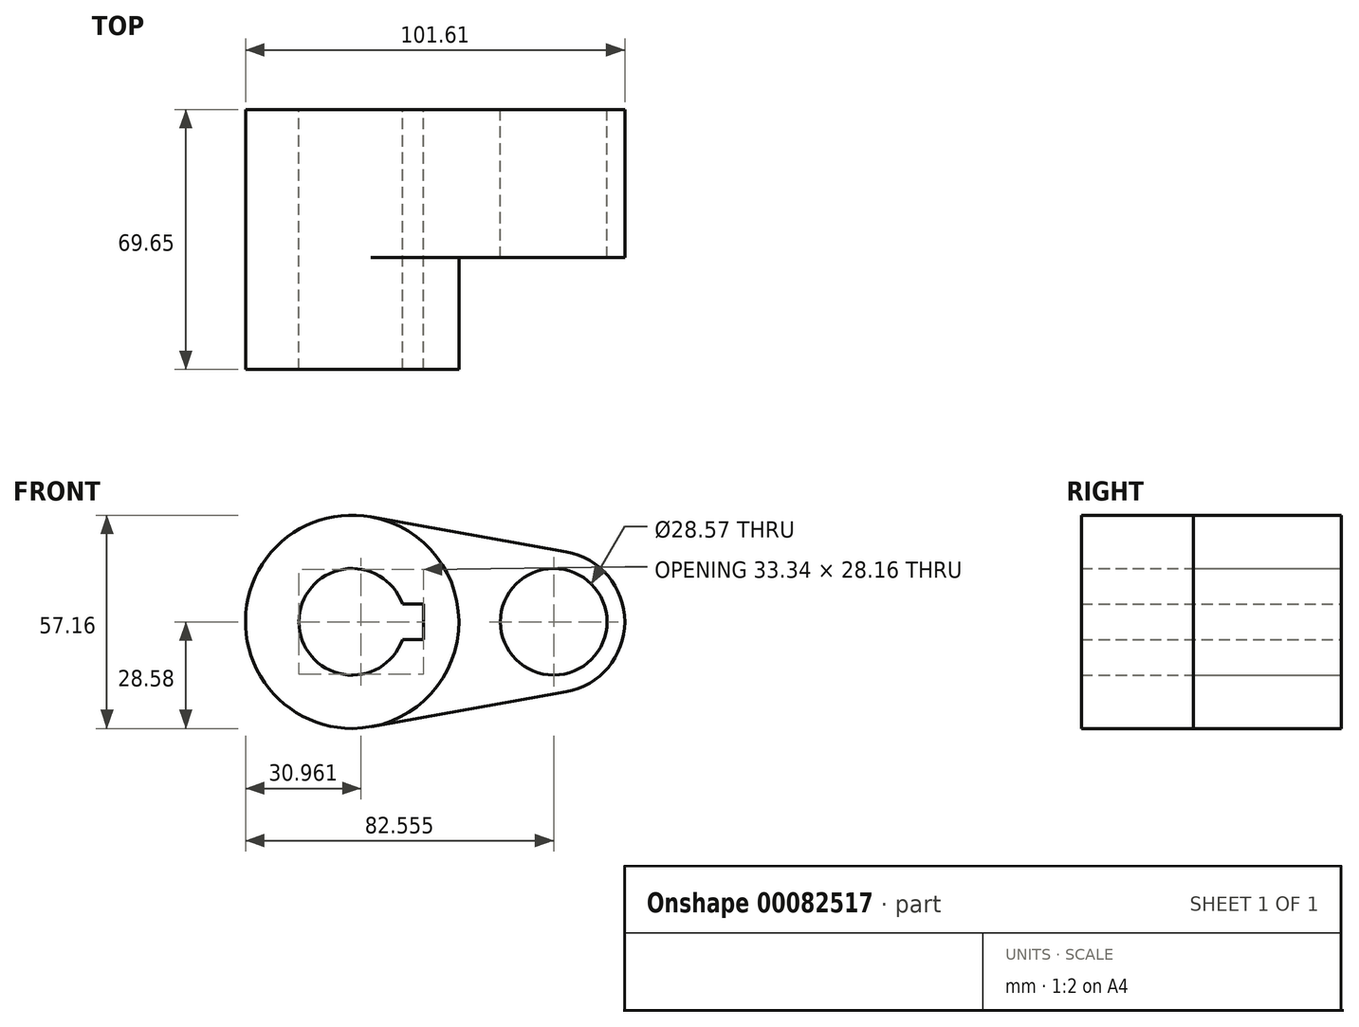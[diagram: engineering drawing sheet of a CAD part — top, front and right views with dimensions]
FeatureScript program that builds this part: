
annotation { "Feature Type Name" : "Feature", "Feature Type Description" : "" }
export const myFeature = defineFeature(function(context is Context, id is Id, definition is map)
    precondition{}
    {
        {
            var Q0;
            Q0=qCreatedBy(makeId("Front.planeOp"),FACE);
            var sketch = newSketch(context, id + "F0", { "sketchPlane" : qUnion([Q0])});
            skCircle(sketch, "E0", {"center": v(0, 0) * mm, "radius": 28.58 * mm});
            skCircle(sketch, "E1", {"center": v(53.98, 0) * mm, "radius": 19.05 * mm});
            skLineSegment(sketch, "E2", {"start": v(5.04, 28.13) * mm, "end": v(57.34, 18.75) * mm});
            skLineSegment(sketch, "E3", {"start": v(5.04, -28.13) * mm, "end": v(57.34, -18.75) * mm});
            skCircle(sketch, "E4", {"center": v(0, 0) * mm, "radius": 14.29 * mm});
            skCircle(sketch, "E5", {"center": v(53.98, 0) * mm, "radius": 14.29 * mm});
            skLineSegment(sketch, "E6.bottom", {"start": v(19.05, -4.76) * mm, "end": v(-19.05, -4.76) * mm});
            skLineSegment(sketch, "E6.top", {"start": v(19.05, 4.76) * mm, "end": v(-19.05, 4.76) * mm});
            skLineSegment(sketch, "E6.left", {"start": v(19.05, -4.76) * mm, "end": v(19.05, 4.76) * mm});
            skLineSegment(sketch, "E6.right", {"start": v(-19.05, -4.76) * mm, "end": v(-19.05, 4.76) * mm});
            skSolve(sketch);
        }
        {
            var Q0;
            {var subQ11=sQuery(id+"F0.wireOp",EDGE,"E6.left");Q0=makeQuery(id+"F0.imprint","IMPRINT",FACE,{"disambiguationData":[TD([[makeQuery(id+"F0.imprint","IMPRINT",EDGE,{"derivedFrom":subQ11}),-1.0]])]});}
            var Q1;
            {var subQ5=sQuery(id+"F0.wireOp",EDGE,"E6.right");Q1=makeQuery(id+"F0.imprint","IMPRINT",FACE,{"disambiguationData":[TD([[makeQuery(id+"F0.imprint","IMPRINT",EDGE,{"derivedFrom":subQ5}),-1.0]])]});}
            var Q2;
            {var subQ0=sQuery(id+"F0.wireOp",EDGE,"E2");Q2=makeQuery(id+"F0.imprint","IMPRINT",FACE,{"disambiguationData":[TD([[makeQuery(id+"F0.imprint","IMPRINT",EDGE,{"derivedFrom":subQ0}),-1.0]])]});}
            var Q3;
            Q3=makeQuery(id+"F0.imprint","IMPRINT",FACE,{"disambiguationData":[TD([[makeQuery(id+"F0.imprint","IMPRINT",EDGE,{"derivedFrom":sQuery(id+"F0.wireOp",EDGE,"E5")}),-1.0]])]});
            extrude(context, id + "F1", {"entities" : qUnion([Q0, Q1, Q2, Q3]), "depth" : 39.66 * mm});
        }
        {
            var Q0;
            {var subQ11=sQuery(id+"F0.wireOp",EDGE,"E6.left");Q0=makeQuery(id+"F0.imprint","IMPRINT",FACE,{"disambiguationData":[TD([[makeQuery(id+"F0.imprint","IMPRINT",EDGE,{"derivedFrom":subQ11}),-1.0]])]});}
            var Q1;
            {var subQ5=sQuery(id+"F0.wireOp",EDGE,"E6.right");Q1=makeQuery(id+"F0.imprint","IMPRINT",FACE,{"disambiguationData":[TD([[makeQuery(id+"F0.imprint","IMPRINT",EDGE,{"derivedFrom":subQ5}),-1.0]])]});}
            extrude(context, id + "F2", {"entities" : qUnion([Q0, Q1]), "operationType" : NewBodyOperationType.ADD, "depth" : 69.65 * mm});
        }
    });
